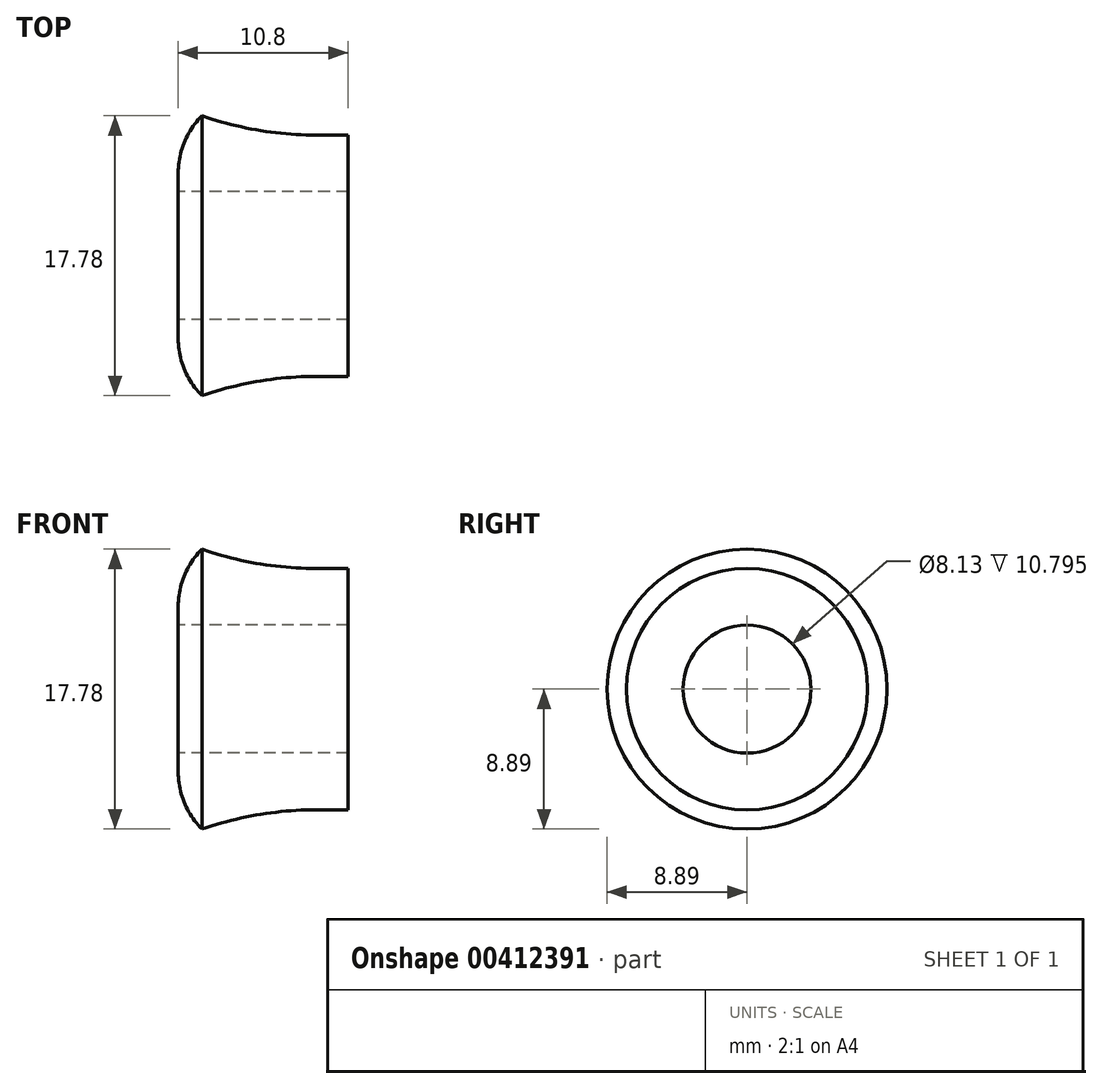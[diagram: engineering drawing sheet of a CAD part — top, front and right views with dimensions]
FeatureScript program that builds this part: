
annotation { "Feature Type Name" : "Feature", "Feature Type Description" : "" }
export const myFeature = defineFeature(function(context is Context, id is Id, definition is map)
    precondition{}
    {
        {
            var Q0;
            Q0=qCreatedBy(makeId("Front.planeOp"),FACE);
            var sketch = newSketch(context, id + "F0", { "sketchPlane" : qUnion([Q0])});
            skLineSegment(sketch, "E0", {"start": v(0, 4.06) * mm, "end": v(0, 8.9) * mm});
            skLineSegment(sketch, "E1", {"start": v(0, 8.9) * mm, "end": v(1.52, 8.9) * mm});
            skLineSegment(sketch, "E2", {"start": v(10.8, 7.66) * mm, "end": v(10.8, 4.06) * mm});
            skLineSegment(sketch, "E3", {"start": v(10.8, 4.06) * mm, "end": v(0, 4.06) * mm});
            skLineSegment(sketch, "E4", {"start": v(0, 0) * mm, "end": v(20.86, 0) * mm, "construction": true});
            skLineSegment(sketch, "E5", {"start": v(10.8, 7.66) * mm, "end": v(8.76, 7.66) * mm});
            skArc(sketch, "E6", {"start": v(1.52, 8.9) * mm, "mid": v(5.1, 7.97) * mm, "end": v(8.76, 7.66) * mm});
            skPoint(sketch, "E7.orphan", {"position": v(0, 3.3) * mm});
            skSolve(sketch);
        }
        {
            var Q0;
            Q0 = qSketchRegion(id + "F0", true);
            var Q1;
            Q1=sQuery(id+"F0.wireOp",EDGE,"E4");
            revolve(context, id + "F1", {"entities" : qUnion([Q0]), "axis" : qUnion([Q1]), "revolveType" : RevolveType.FULL});
        }
        {
            var Q0;
            Q0=makeQuery(id+"F1.opRevolve","SWEPT_EDGE",EDGE,{"disambiguationData":[OSD([sQuery(id+"F0.wireOp",EDGE,"E0"),sQuery(id+"F0.wireOp",EDGE,"E1")])]});
            fillet(context, id + "F2", {"entities" : qUnion([Q0]), "radius" : 5.08 * mm, "tangentPropagation" : true, "allowEdgeOverflow" : false});
        }
    });
